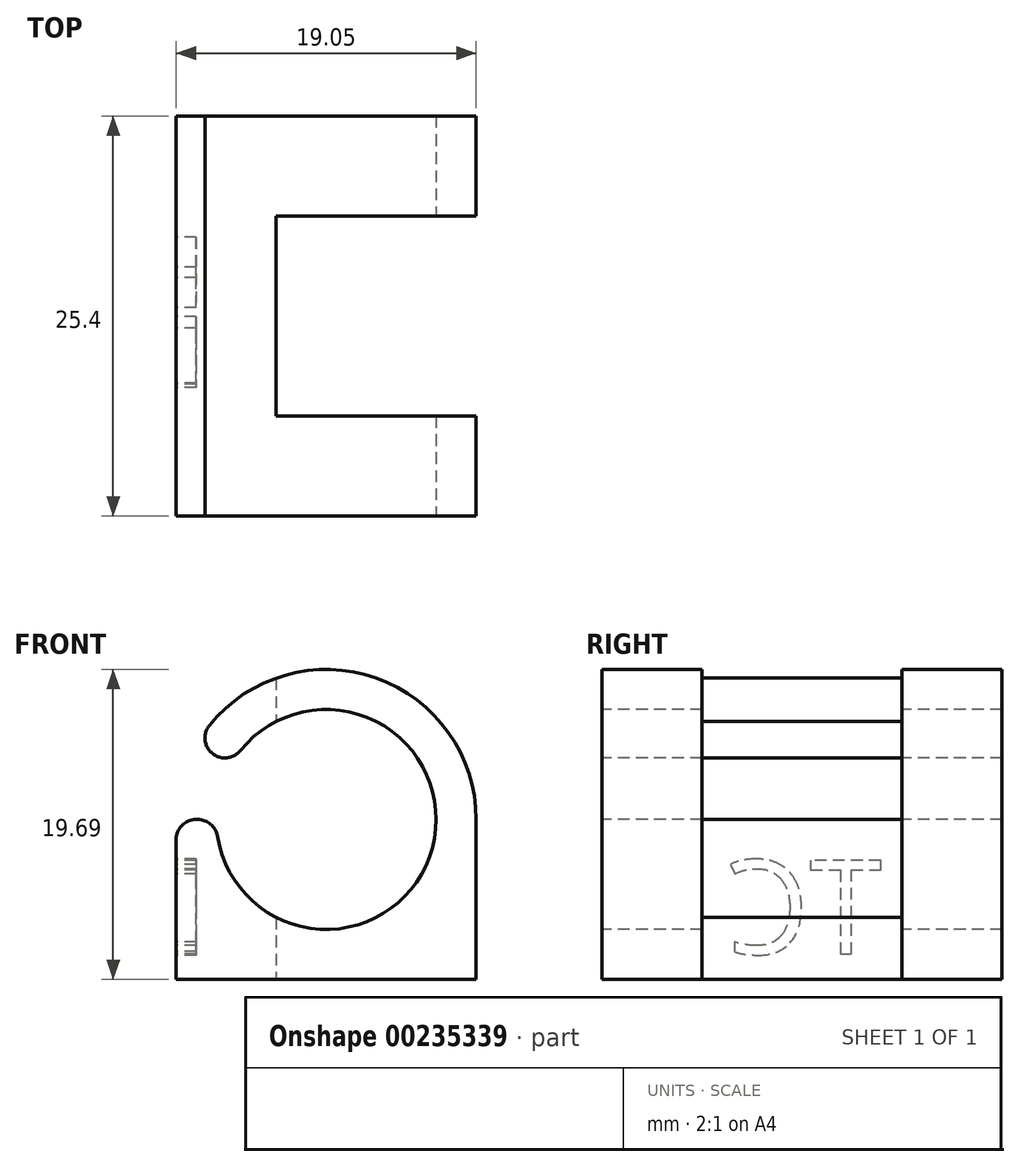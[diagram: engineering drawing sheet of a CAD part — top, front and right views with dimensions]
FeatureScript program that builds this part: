
annotation { "Feature Type Name" : "Feature", "Feature Type Description" : "" }
export const myFeature = defineFeature(function(context is Context, id is Id, definition is map)
    precondition{}
    {
        {
            var Q0;
            Q0=qCreatedBy(makeId("Top.planeOp"),FACE);
            var sketch = newSketch(context, id + "F0", { "sketchPlane" : qUnion([Q0])});
            skLineSegment(sketch, "E0.bottom", {"start": v(0, 0) * mm, "end": v(19.05, 0) * mm});
            skLineSegment(sketch, "E0.top", {"start": v(0, 25.4) * mm, "end": v(19.05, 25.4) * mm});
            skLineSegment(sketch, "E0.left", {"start": v(0, 0) * mm, "end": v(0, 25.4) * mm});
            skLineSegment(sketch, "E0.right", {"start": v(19.05, 0) * mm, "end": v(19.05, 25.4) * mm});
            skSolve(sketch);
        }
        {
            var Q0;
            Q0 = qSketchRegion(id + "F0", true);
            extrude(context, id + "F1", {"entities" : qUnion([Q0]), "depth" : 3.17 * mm});
        }
        {
            var Q0;
            Q0=makeQuery(id+"F1.opExtrude","SWEPT_FACE",FACE,{"disambiguationData":[OSD([sQuery(id+"F0.wireOp",EDGE,"E0.bottom")])]});
            var sketch = newSketch(context, id + "F2", { "sketchPlane" : qUnion([Q0])});
            skLineSegment(sketch, "E1", {"start": v(19.05, 3.18) * mm, "end": v(19.05, 10.16) * mm});
            skArc(sketch, "E2", {"start": v(19.05, 10.16) * mm, "mid": v(12, 19.36) * mm, "end": v(1.28, 14.92) * mm});
            skLineSegment(sketch, "E3", {"start": v(1.28, 14.92) * mm, "end": v(3.48, 13.65) * mm});
            skArc(sketch, "E4", {"start": v(2.54, 10.16) * mm, "mid": v(16.27, 8.35) * mm, "end": v(3.48, 13.65) * mm});
            skLineSegment(sketch, "E5", {"start": v(9.53, 3.18) * mm, "end": v(9.53, 10.16) * mm, "construction": true});
            skLineSegment(sketch, "E6", {"start": v(9.53, 10.16) * mm, "end": v(1.28, 14.92) * mm, "construction": true});
            skLineSegment(sketch, "E7", {"start": v(0, 10.16) * mm, "end": v(0, 3.18) * mm});
            skLineSegment(sketch, "E8", {"start": v(0, 3.18) * mm, "end": v(19.05, 3.18) * mm});
            skLineSegment(sketch, "E9", {"start": v(2.54, 10.16) * mm, "end": v(0, 10.16) * mm});
            skLineSegment(sketch, "E10", {"start": v(9.52, 10.16) * mm, "end": v(0, 10.16) * mm, "construction": true});
            skSolve(sketch);
        }
        {
            var Q0;
            Q0 = qSketchRegion(id + "F2", true);
            var Q1;
            Q1=makeQuery(id+"F1.opExtrude","SWEPT_FACE",FACE,{"disambiguationData":[OSD([sQuery(id+"F0.wireOp",EDGE,"E0.top")])]});
            extrude(context, id + "F3", {"entities" : qUnion([Q0]), "operationType" : NewBodyOperationType.ADD, "endBound" : BoundingType.UP_TO_SURFACE, "oppositeDirection" : true, "endBoundEntityFace" : qUnion([Q1]), "depth" : 25.4 * mm});
        }
        {
            var Q0;
            Q0=makeQuery(id+"F3.opExtrude","SWEPT_EDGE",EDGE,{"disambiguationData":[OSD([sQuery(id+"F2.wireOp",EDGE,"E2"),sQuery(id+"F2.wireOp",EDGE,"E3")])]});
            var Q1;
            Q1=makeQuery(id+"F3.opExtrude","SWEPT_EDGE",EDGE,{"disambiguationData":[OSD([sQuery(id+"F2.wireOp",EDGE,"E3"),sQuery(id+"F2.wireOp",EDGE,"E4")])]});
            var Q2;
            Q2=makeQuery(id+"F3.opExtrude","SWEPT_EDGE",EDGE,{"disambiguationData":[OSD([sQuery(id+"F2.wireOp",EDGE,"E4"),sQuery(id+"F2.wireOp",EDGE,"E9")])]});
            var Q3;
            Q3=makeQuery(id+"F3.opExtrude","SWEPT_EDGE",EDGE,{"disambiguationData":[OSD([sQuery(id+"F2.wireOp",EDGE,"E7"),sQuery(id+"F2.wireOp",EDGE,"E9")])]});
            fillet(context, id + "F4", {"entities" : qUnion([Q0, Q1, Q2, Q3]), "radius" : 1.27 * mm, "tangentPropagation" : true, "allowEdgeOverflow" : false});
        }
        {
            var Q0;
            Q0=makeQuery(id+"F1.opExtrude","CAP_FACE",FACE,{"disambiguationData":[OSD([sQuery(id+"F0.wireOp",EDGE,"E0.bottom"),sQuery(id+"F0.wireOp",EDGE,"E0.top"),sQuery(id+"F0.wireOp",EDGE,"E0.left"),sQuery(id+"F0.wireOp",EDGE,"E0.right")])],"isStart":true});
            var sketch = newSketch(context, id + "F5", { "sketchPlane" : qUnion([Q0])});
            skLineSegment(sketch, "E11.bottom", {"start": v(19.05, -6.35) * mm, "end": v(6.35, -6.35) * mm});
            skLineSegment(sketch, "E11.top", {"start": v(19.05, -19.05) * mm, "end": v(6.35, -19.05) * mm});
            skLineSegment(sketch, "E11.left", {"start": v(19.05, -6.35) * mm, "end": v(19.05, -19.05) * mm});
            skLineSegment(sketch, "E11.right", {"start": v(6.35, -6.35) * mm, "end": v(6.35, -19.05) * mm});
            skLineSegment(sketch, "E12", {"start": v(6.35, -19.05) * mm, "end": v(19.05, -25.4) * mm, "construction": true});
            skLineSegment(sketch, "E13", {"start": v(6.35, -6.35) * mm, "end": v(19.05, 0) * mm, "construction": true});
            skSolve(sketch);
        }
        {
            var Q0;
            Q0 = qSketchRegion(id + "F5", true);
            extrude(context, id + "F6", {"entities" : qUnion([Q0]), "operationType" : NewBodyOperationType.REMOVE, "endBound" : BoundingType.THROUGH_ALL, "oppositeDirection" : true, "depth" : 25.4 * mm});
        }
        {
            var Q0;
            Q0=makeQuery(id+"F3.boolean.opBoolean","MERGE",FACE,{"derivedFrom":[makeQuery(id+"F1.opExtrude","SWEPT_FACE",FACE,{"disambiguationData":[OSD([sQuery(id+"F0.wireOp",EDGE,"E0.left")])]}),makeQuery(id+"F3.opExtrude","SWEPT_FACE",FACE,{"disambiguationData":[OSD([sQuery(id+"F2.wireOp",EDGE,"E7")])]})]});
            var sketch = newSketch(context, id + "F7", { "sketchPlane" : qUnion([Q0])});
            skText(sketch, "E14", { "text": "TC", "fontName": "OpenSans-Regular.ttf"});
            skLineSegment(sketch, "E15", {"start": v(-17.78, 1.62) * mm, "end": v(-25.4, 0) * mm, "construction": true});
            skLineSegment(sketch, "E16", {"start": v(-7.62, 1.62) * mm, "end": v(0, 0) * mm, "construction": true});
            const initialGuessF7  = {"E14": [-0.01778, 0.00162, 1, 0, 0.006]};
            skSetInitialGuess(sketch, initialGuessF7);
            skSolve(sketch);
        }
        {
            var Q0;
            Q0 = qSketchRegion(id + "F7", true);
            extrude(context, id + "F8", {"entities" : qUnion([Q0]), "operationType" : NewBodyOperationType.REMOVE, "oppositeDirection" : true, "depth" : 1.27 * mm});
        }
    });
